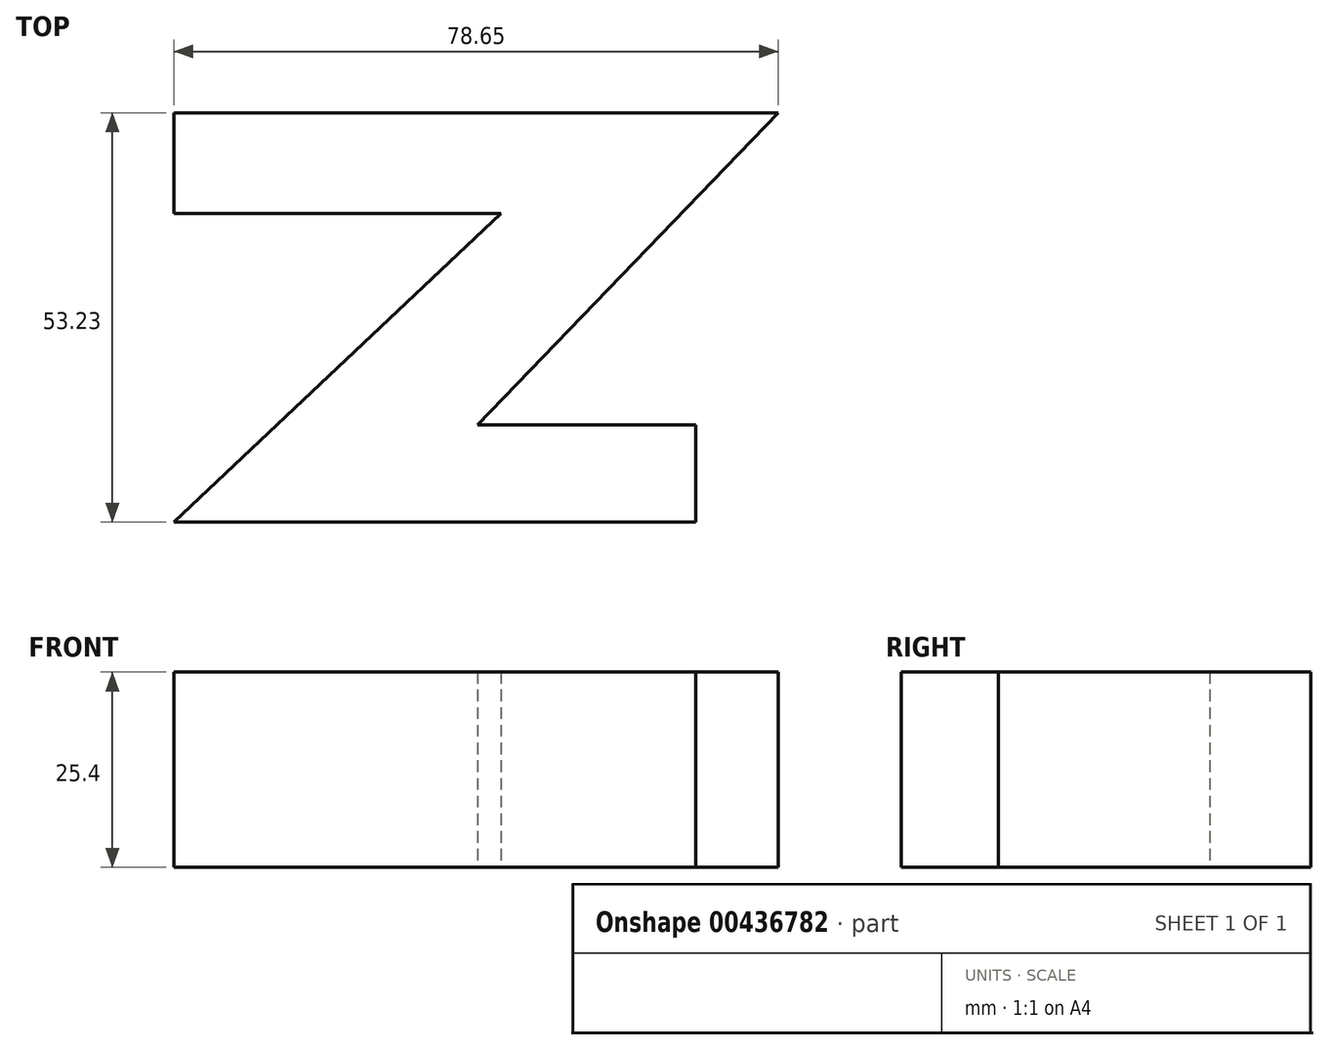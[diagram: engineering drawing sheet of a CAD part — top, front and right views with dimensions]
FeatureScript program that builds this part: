
annotation { "Feature Type Name" : "Feature", "Feature Type Description" : "" }
export const myFeature = defineFeature(function(context is Context, id is Id, definition is map)
    precondition{}
    {
        {
            var Q0;
            Q0=qCreatedBy(makeId("Top.planeOp"),FACE);
            var sketch = newSketch(context, id + "F0", { "sketchPlane" : qUnion([Q0])});
            skLineSegment(sketch, "E0", {"start": v(-20.91, 40.13) * mm, "end": v(21.64, 40.13) * mm});
            skLineSegment(sketch, "E1", {"start": v(21.64, 40.13) * mm, "end": v(-20.91, 0) * mm});
            skLineSegment(sketch, "E2", {"start": v(-20.91, 0) * mm, "end": v(21.64, 0) * mm});
            skLineSegment(sketch, "E3", {"start": v(-20.91, 40.13) * mm, "end": v(-20.91, 53.23) * mm});
            skLineSegment(sketch, "E4", {"start": v(-20.91, 53.23) * mm, "end": v(57.74, 53.23) * mm});
            skLineSegment(sketch, "E5", {"start": v(57.74, 53.23) * mm, "end": v(18.58, 12.61) * mm});
            skLineSegment(sketch, "E6", {"start": v(18.58, 12.61) * mm, "end": v(47, 12.61) * mm});
            skLineSegment(sketch, "E7", {"start": v(47, 12.61) * mm, "end": v(47, 0) * mm});
            skLineSegment(sketch, "E8", {"start": v(47, 0) * mm, "end": v(-20.91, 0) * mm});
            skSolve(sketch);
        }
        {
            var Q0;
            Q0 = qSketchRegion(id + "F0", true);
            var Q1;
            Q1=makeQuery(id+"F0.imprint","IMPRINT",FACE,{"disambiguationData":[TD([[makeQuery(id+"F0.imprint","IMPRINT",EDGE,{"derivedFrom":sQuery(id+"F0.wireOp",EDGE,"E0")}),1.0]])]});
            extrude(context, id + "F1", {"entities" : qUnion([Q0, Q1]), "depth" : 25.4 * mm});
        }
    });
